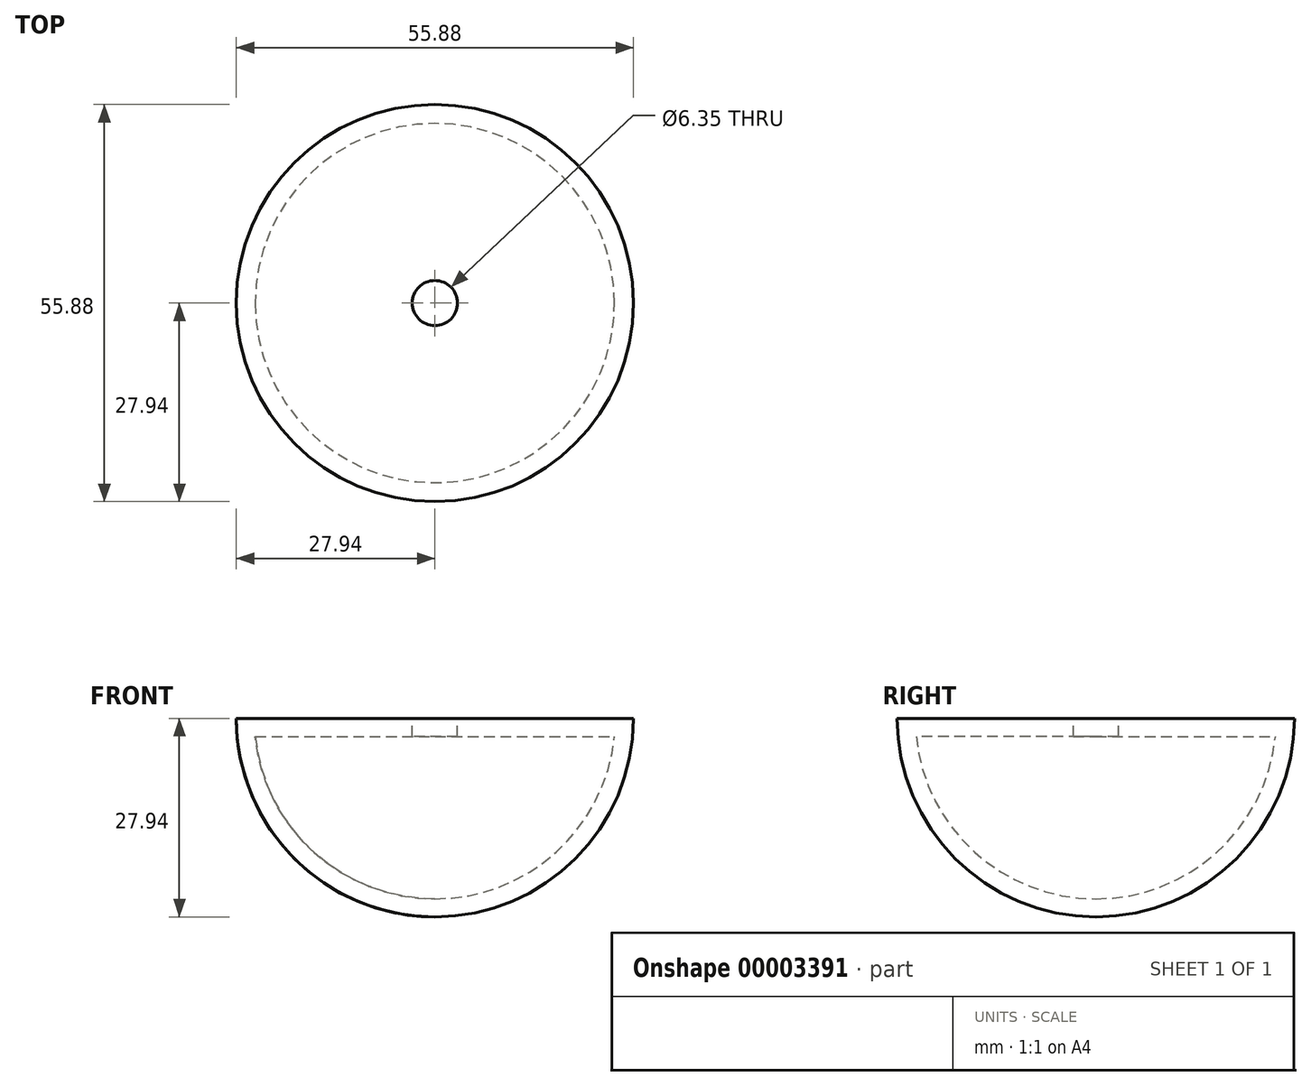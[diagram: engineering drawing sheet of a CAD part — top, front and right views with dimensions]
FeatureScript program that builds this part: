
annotation { "Feature Type Name" : "Feature", "Feature Type Description" : "" }
export const myFeature = defineFeature(function(context is Context, id is Id, definition is map)
    precondition{}
    {
        {
            var Q0;
            Q0=qCreatedBy(makeId("Front.planeOp"),FACE);
            var sketch = newSketch(context, id + "F0", { "sketchPlane" : qUnion([Q0])});
            skArc(sketch, "E0", {"start": v(-27.94, 0) * mm, "mid": v(-19.76, -19.76) * mm, "end": v(0, -27.94) * mm});
            skLineSegment(sketch, "E1", {"start": v(-27.94, 0) * mm, "end": v(-25.4, 0) * mm});
            skArc(sketch, "E2", {"start": v(-25.27, -2.54) * mm, "mid": v(-17.04, -18.84) * mm, "end": v(0, -25.4) * mm});
            skLineSegment(sketch, "E3", {"start": v(0, -27.94) * mm, "end": v(0, -25.4) * mm});
            skPoint(sketch, "E4.orphan", {"position": v(0, -34.02) * mm});
            skLineSegment(sketch, "E5.bottom", {"start": v(-25.4, 0) * mm, "end": v(-3.18, 0) * mm});
            skLineSegment(sketch, "E5.top", {"start": v(-25.27, -2.54) * mm, "end": v(-3.18, -2.54) * mm});
            skLineSegment(sketch, "E5.right", {"start": v(-3.18, 0) * mm, "end": v(-3.18, -2.54) * mm});
            skSolve(sketch);
        }
        {
            var Q0;
            Q0=qCreatedBy(makeId("Front.planeOp"),FACE);
            var sketch = newSketch(context, id + "F1", { "sketchPlane" : qUnion([Q0])});
            skLineSegment(sketch, "E6", {"start": v(0, 36.33) * mm, "end": v(0, -35.7) * mm});
            skSolve(sketch);
        }
        {
            var Q0;
            Q0=makeQuery(id+"F0.imprint","IMPRINT",FACE,{"disambiguationData":[TD([[makeQuery(id+"F0.imprint","IMPRINT",EDGE,{"derivedFrom":sQuery(id+"F0.wireOp",EDGE,"E0")}),1.0]])]});
            var Q1;
            Q1=sQuery(id+"F1.wireOp",EDGE,"E6");
            revolve(context, id + "F2", {"entities" : qUnion([Q0]), "axis" : qUnion([Q1]), "revolveType" : RevolveType.FULL});
        }
    });
